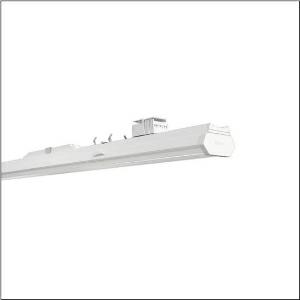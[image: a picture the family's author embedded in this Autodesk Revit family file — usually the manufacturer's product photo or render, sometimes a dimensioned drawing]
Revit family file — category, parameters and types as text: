
# Revit family: licross_r__21_protected_mo_52td117n485g_f66a
name_source: partatom
category: Lighting Fixtures
units: mm (PartAtom-declared; Revit-internal decimal feet)

## family parameters
Cut with Voids When Loaded = No
Host = Face
Light Source = No
Part Type = Normal
Room Calculation Point = No
Round Connector Dimension = Use Diameter
Shared = No

## types (1)
- Licross® 21 Protected MO (1 x LED, 8570 lm, 47.9 W, 4000K)
    Apparent Load = 48 VA
    CIE Flux Codes = 83 94 98 100 100
    Color Rendering = 80
    Color Temperature = 4000K
    Default Elevation = 1800 mm
    Description = Licross® 21 Protected MO, luminaire insert, of sheet steel, galvanised, coil coated, white, length: 1.500mm, width: 66mm, height: 67mm, LED rated luminous flux: 8.570lm, light colour: 840, control gear: ON/OFF, with plug, 3-pole, with phase selection, mains connection: 220..240V, AC, 50/60Hz, rated input power: 48W, internal wiring halogen-free, primary light control with lens, of plastic, primary optical cover: cover, of PMMA, light emission: direct distribution, primary light characteristic: symmetric, protection rating (complete): IP54, insulation class (complete): insulation class I (protective earthing), certification: CE, ENEC, VDE, UKCA, protection symbol: D if used in an environment with non-conductive dust loads with corresponding accessories, impact resistance: IK06, permissible ambient temperature for indoor applications: -35..+45°C, corresponds to IFS (International Featured Standards) requirements for safety and quality in the food industry, reducing of maximum allowable ambient temperature of 5°C with ceiling mounting, LABS conformity tested according to VDMA 24364:2018-05, packaging unit: 1 piece
    Height = 92 mm
    Lamp = 1 x LED
    Lamp Light Flux = 8570 lm
    Lamp Power = 47.9 W
    Lamp count = 1
    Length = 1500 mm
    Luminous efficacy = 179 lm/W
    Manufacturer = Siteco
    ModVariant = No
    Model = 52TD117N485G
    Mounting Place = Ceiling
    Mounting Type = Pendant
    Number of Poles = 1
    OnlyDefault = Yes
    Power Factor = 1
    Product Name = Licross® 21 Protected MO
    Product group = luminaire insert | ceiling pendant
    ProductGroupID = 902
    Protection Class = Protection class I
    Protection Degree = IP 54
    RLX_Detail_Level = 1
    RLX_Emergency_Light_Flux = 0 lm
    RLX_Emergency_Type = 0
    RLX_Emergency_Type_DB = No
    RlxData = <blob elided: 20393 chars, md5=6f96cc5a>
    Socket = socket
    Standby Power = 0 W
    System Light Flux = 8570 lm
    System Power = 48 W
    Type Comments = Product without accessories
    Type Image = l_1256148.jpg
    URL = http://relux.com
    VarID = ---
    Voltage = 0 V
    Weight = 0.00 kg
    Width = 88 mm

## geometry (parser evidence)
native form markers: Blend x4, Sweep x12
no freeform markers — native parametric forms only
